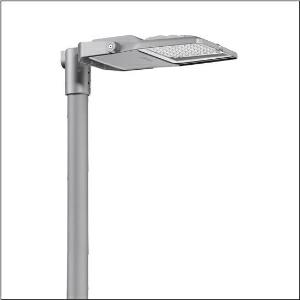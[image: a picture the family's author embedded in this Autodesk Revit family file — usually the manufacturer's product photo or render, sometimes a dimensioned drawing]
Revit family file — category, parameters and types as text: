
# Revit family: floodlight_fl_21_mini___pl61_5xa7775c2c3a_8aba
name_source: partatom
category: Lighting Fixtures
units: mm (PartAtom-declared; Revit-internal decimal feet)

## family parameters
Cut with Voids When Loaded = No
Host = Face
Light Source = No
Part Type = Normal
Room Calculation Point = No
Round Connector Dimension = Use Diameter
Shared = No

## types (1)
- --- (1 x LED, 11960 lm, 89 W, 3000K)
    Apparent Load = 89 VA
    CIE Flux Codes = 33 65 98 100 100
    Color Rendering = 70
    Color Temperature = 3000K
    Default Elevation = 1800 mm
    Description = Floodlight FL 21 mini, floodlight, primary light control with lens, of PMMA, primary optical cover: protective disc, of toughened safety glass, transparent, light distribution: PL61, light emission: direct distribution, installation type: surface-mounted, LED, High Power LED, rated luminous flux: 11.960lm, luminous efficacy: 134lm/W, light colour: 730, colour temperature: 3000K, control: flexible luminous flux parameterisation, time-dependent luminous flux control, constant luminous flux control, overheat protection, presetting dimming logarithmic, with terminal, 6-pole, mains connection: 220..240V, AC, 50/60Hz, start of lifetime: 89W, end of service life: 94W, reduction: 43W, luminaire housing, of diecast aluminium, powder-coated, Siteco® metallic grey (DB 702S), corrosivity category C5 mid according to DIN EN ISO 12944, sealing non-destructively replaceable, please order mast flange separately, mast bracket, of steel, galvanised, powder-coated, Siteco® metallic grey (DB 702S), Smart Interface above, protection rating (complete): IP66, insulation class (complete): insulation class II (safety insulation), certification: CE, ENEC, VDE, protection symbol: D, impact resistance: IK08, permissible operating ambient temperature: -40..+40°C, permissible operating ambient temperature for outdoor applications: -40..+50°C, standard: DIN EN 12944, LABS conformity tested according to VDMA 24364:2018-05, packaging unit: 1 piece

Light Distribution: PL61
    Height = 70 mm
    Lamp = 1 x LED
    Lamp Light Flux = 11960 lm
    Lamp Power = 89 W
    Lamp count = 1
    Length = 485 mm
    Luminous efficacy = 134 lm/W
    Manufacturer = Siteco
    ModVariant = No
    Model = 5XA7775C2C3A
    Number of Poles = 1
    OnlyDefault = Yes
    Power Factor = 1
    Product Name = Floodlight FL 21 mini | PL61
    Product group = floodlight | pylon annexe
    ProductGroupID = 6200
    Protection Class = Protection class II
    Protection Degree = IP 66
    RLX_Detail_Level = 1
    RLX_Emergency_Light_Flux = 0 lm
    RLX_Emergency_Type = 0
    RLX_Emergency_Type_DB = No
    RlxData = <blob elided: 100905 chars, md5=98bb8e76>
    Socket = socket
    Standby Power = 0 W
    System Light Flux = 11960 lm
    System Power = 89 W
    Type Comments = factory setting: luminous flux: 100 % | dim-lin: 254 | 456 mA
    Type Image = l_1007125.jpg
    URL = http://relux.com
    VarID = @adj_122989
    Voltage = 0 V
    Weight = 0.00 kg
    Width = 337 mm

## geometry (parser evidence)
native form markers: Blend x4, Sweep x13
no freeform markers — native parametric forms only
